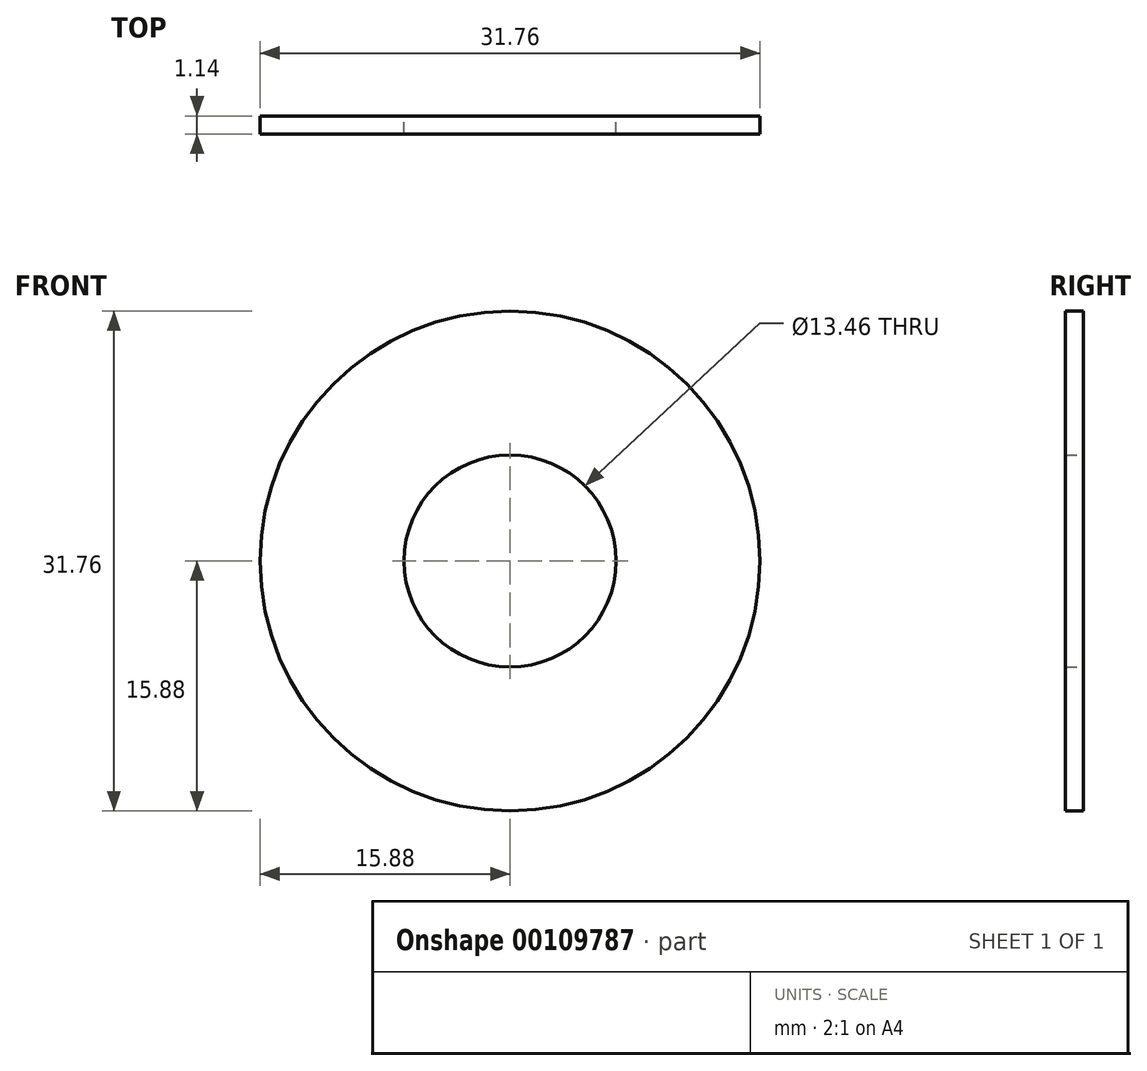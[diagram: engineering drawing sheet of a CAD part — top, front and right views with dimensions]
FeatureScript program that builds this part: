
annotation { "Feature Type Name" : "Feature", "Feature Type Description" : "" }
export const myFeature = defineFeature(function(context is Context, id is Id, definition is map)
    precondition{}
    {
        {
            var Q0;
            Q0=qCreatedBy(makeId("Front.planeOp"),FACE);
            var sketch = newSketch(context, id + "F0", { "sketchPlane" : qUnion([Q0])});
            skCircle(sketch, "E0", {"center": v(0, 0) * mm, "radius": 15.88 * mm});
            skCircle(sketch, "E1", {"center": v(0, 0) * mm, "radius": 6.73 * mm});
            skSolve(sketch);
        }
        {
            var Q0;
            Q0 = qSketchRegion(id + "F0", true);
            extrude(context, id + "F1", {"entities" : qUnion([Q0]), "depth" : 1.14 * mm});
        }
    });
